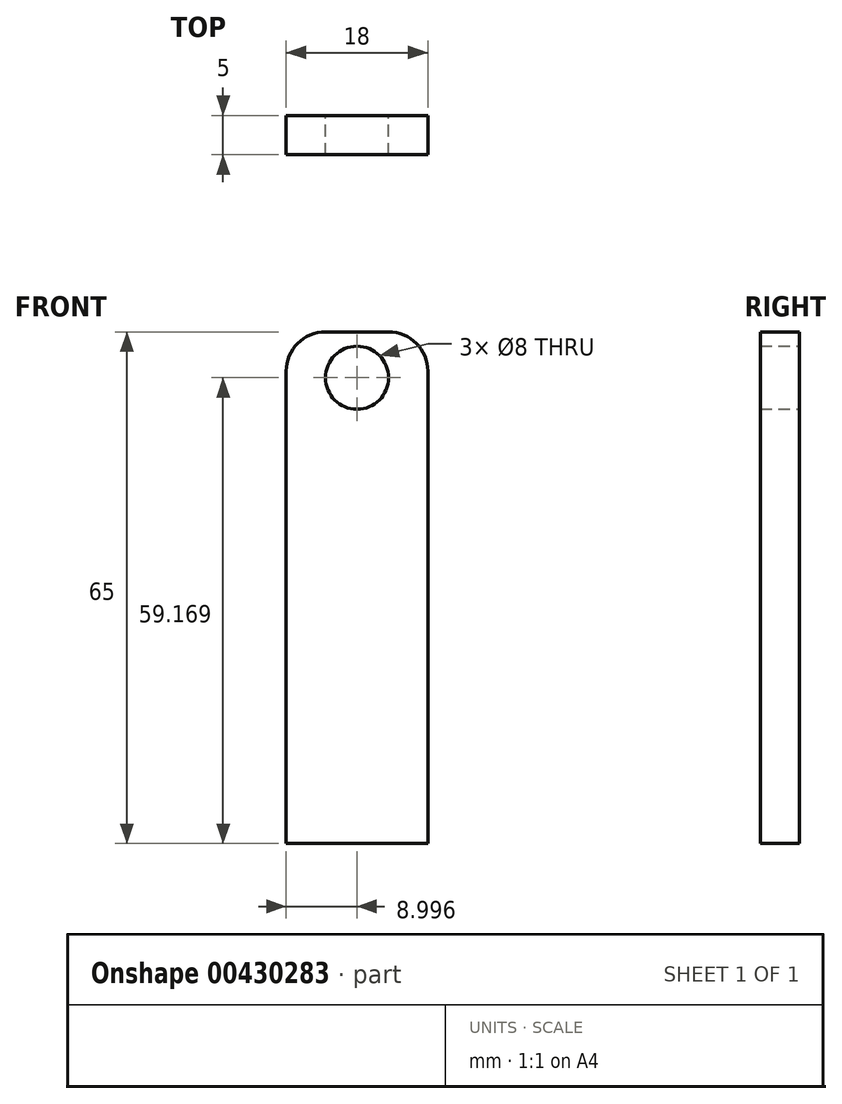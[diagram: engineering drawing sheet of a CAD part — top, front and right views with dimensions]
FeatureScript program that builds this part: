
annotation { "Feature Type Name" : "Feature", "Feature Type Description" : "" }
export const myFeature = defineFeature(function(context is Context, id is Id, definition is map)
    precondition{}
    {
        {
            var Q0;
            Q0=qCreatedBy(makeId("Front.planeOp"),FACE);
            var sketch = newSketch(context, id + "F0", { "sketchPlane" : qUnion([Q0])});
            skLineSegment(sketch, "E0.bottom", {"start": v(-44.72, 17.98) * mm, "end": v(-26.72, 17.98) * mm});
            skLineSegment(sketch, "E0.top", {"start": v(-44.72, -47.02) * mm, "end": v(-26.72, -47.02) * mm});
            skLineSegment(sketch, "E0.left", {"start": v(-44.72, 17.98) * mm, "end": v(-44.72, -47.02) * mm});
            skLineSegment(sketch, "E0.right", {"start": v(-26.72, 17.98) * mm, "end": v(-26.72, -47.02) * mm});
            skPoint(sketch, "E1", {"position": v(-35.72, 12.15) * mm});
            skCircle(sketch, "E2", {"center": v(-35.72, 12.15) * mm, "radius": 4 * mm});
            skSolve(sketch);
        }
        {
            var Q0;
            Q0=makeQuery(id+"F0.imprint","IMPRINT",FACE,{"disambiguationData":[TD([[makeQuery(id+"F0.imprint","IMPRINT",EDGE,{"derivedFrom":sQuery(id+"F0.wireOp",EDGE,"E0.bottom")}),-1.0]])]});
            extrude(context, id + "F1", {"entities" : qUnion([Q0]), "depth" : 5 * mm});
        }
        {
            var Q0;
            Q0=makeQuery(id+"F1.opExtrude","SWEPT_EDGE",EDGE,{"disambiguationData":[OSD([sQuery(id+"F0.wireOp",EDGE,"E0.bottom"),sQuery(id+"F0.wireOp",EDGE,"E0.left")])]});
            var Q1;
            Q1=makeQuery(id+"F1.opExtrude","SWEPT_EDGE",EDGE,{"disambiguationData":[OSD([sQuery(id+"F0.wireOp",EDGE,"E0.bottom"),sQuery(id+"F0.wireOp",EDGE,"E0.right")])]});
            fillet(context, id + "F2", {"entities" : qUnion([Q0, Q1]), "radius" : 5 * mm, "tangentPropagation" : true, "allowEdgeOverflow" : false});
        }
    });
